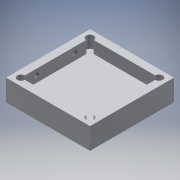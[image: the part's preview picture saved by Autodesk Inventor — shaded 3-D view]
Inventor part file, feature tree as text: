
AUTODESK INVENTOR PART (.ipt)
format: ipt  version: 2017 (Build 210142000, 142)  size: 159,232 bytes
history: native  units: mm
features: sketch x7, hole x4, extrude x3, projected_geometry x3, other x1, split x1
ambient origin geometry x8: Origin, YZ Plane, XZ Plane, XY Plane, X Axis, Y Axis, Z Axis, Center Point
bodies: Body1 (feature_tree)
feature tree (19):
  extrude  "Extrusion1"  Depth=55.0mm
  hole  "Hole2"  [1 undecoded]
  extrude  "Extrusion3"  Depth=8.0mm TaperAngle=0.0deg
  hole  "Hole3"  [1 undecoded]
  extrude  "Extrusion4"  Depth=8.0mm
  hole  "Hole5"  [1 undecoded]
  hole  "Hole6"  [1 undecoded]
  other  "SplitPLane"
  split  "Split2"
  sketch  "Sketch1"  dims[d0=55.0mm d1=55.0mm]
  sketch  "Sketch4"  dims[d2=20.0mm d3=0.0mm d15=45.2mm]
  sketch  "Sketch5"  dims[d16=45.2mm]
  sketch  "Sketch6"  dims[d17=5.0mm d18=6.0mm d19=4.0mm d20=2.0mm d21=90.0deg d22=8.0mm d23=0.0mm d24=8.0mm d25=0.0mm]
  projected_geometry  "Projected Loop1"
  sketch  "Sketch8"  dims[d26=15.0mm d27=15.0mm]
  projected_geometry  "Projected Loop2"
  sketch  "Sketch9"  dims[d28=3.242mm d29=6.0mm d30=4.0mm d31=2.0mm d32=90.0deg d33=8.0mm d34=20.594885mm d44=25.0mm]
  projected_geometry  "Projected Loop3"
  sketch  "Sketch10"  dims[d45=25.0mm d46=6.0mm d47=0.0mm d48=3.0mm d49=6.0mm d50=4.0mm d51=2.0mm d52=90.0deg d53=6.0mm d54=0.0mm d55=3.242mm d56=8.0mm d57=4.0mm d58=2.0mm d59=90.0deg d60=4.0mm d61=20.594885mm d62=0.0mm]
note: 4 required parameter values undecoded (feature->parameter linkage not recoverable at this tier; creation-order binding heuristic only, values carry confidence <= 0.55)
